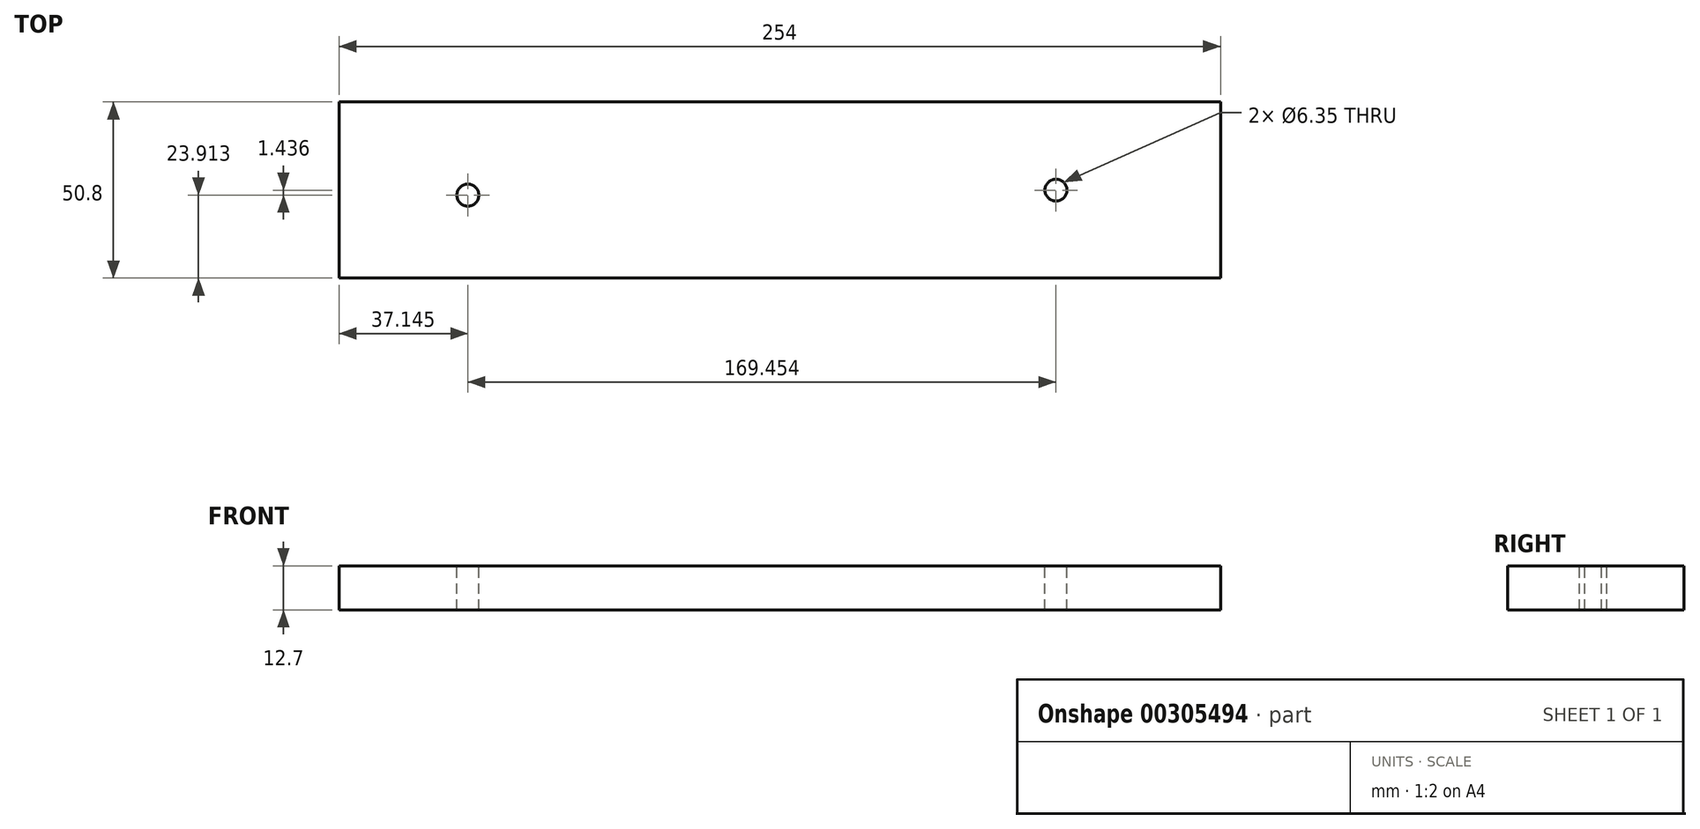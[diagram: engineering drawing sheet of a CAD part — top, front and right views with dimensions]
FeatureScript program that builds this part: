
annotation { "Feature Type Name" : "Feature", "Feature Type Description" : "" }
export const myFeature = defineFeature(function(context is Context, id is Id, definition is map)
    precondition{}
    {
        {
            var Q0;
            Q0=qCreatedBy(makeId("Top.planeOp"),FACE);
            var sketch = newSketch(context, id + "F0", { "sketchPlane" : qUnion([Q0])});
            skLineSegment(sketch, "E0.bottom", {"start": v(0, 50.8) * mm, "end": v(254, 50.8) * mm});
            skLineSegment(sketch, "E0.top", {"start": v(0, 0) * mm, "end": v(254, 0) * mm});
            skLineSegment(sketch, "E0.left", {"start": v(0, 50.8) * mm, "end": v(0, 0) * mm});
            skLineSegment(sketch, "E0.right", {"start": v(254, 50.8) * mm, "end": v(254, 0) * mm});
            skSolve(sketch);
        }
        {
            var Q0;
            Q0 = qSketchRegion(id + "F0", true);
            extrude(context, id + "F1", {"entities" : qUnion([Q0]), "depth" : 12.7 * mm});
        }
        {
            var Q0;
            Q0=makeQuery(id+"F1.opExtrude","CAP_FACE",FACE,{"disambiguationData":[OSD([sQuery(id+"F0.wireOp",EDGE,"E0.bottom"),sQuery(id+"F0.wireOp",EDGE,"E0.top"),sQuery(id+"F0.wireOp",EDGE,"E0.left"),sQuery(id+"F0.wireOp",EDGE,"E0.right")])],"isStart":false});
            var sketch = newSketch(context, id + "F2", { "sketchPlane" : qUnion([Q0])});
            skPoint(sketch, "E1", {"position": v(37.14, 23.91) * mm});
            skPoint(sketch, "E2", {"position": v(206.6, 25.35) * mm});
            skSolve(sketch);
        }
        {
            var Q0;
            Q0=sQuery(id+"F2.wireOp",VERTEX,"E1");
            var Q1;
            Q1=sQuery(id+"F2.wireOp",VERTEX,"E2");
            var Q2;
            Q2=makeQuery(id+"F1.opExtrude","SWEPT_BODY",BODY,{"disambiguationData":[OSD([sQuery(id+"F0.wireOp",EDGE,"E0.bottom"),sQuery(id+"F0.wireOp",EDGE,"E0.top"),sQuery(id+"F0.wireOp",EDGE,"E0.left"),sQuery(id+"F0.wireOp",EDGE,"E0.right")])]});
            hole(context, id + "F3", {"style" : HoleStyle.SIMPLE, "endStyle" : HoleEndStyle.THROUGH, "holeDiameter" : 6.35 * mm, "tappedDepth" : 12.7 * mm, "tapClearance" : 3, "locations" : qUnion([Q0, Q1]), "scope" : qUnion([Q2])});
        }
    });
